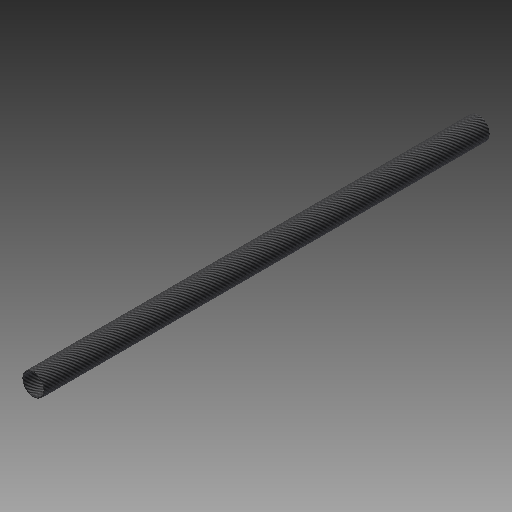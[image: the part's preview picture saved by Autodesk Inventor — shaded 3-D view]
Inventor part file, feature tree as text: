
AUTODESK INVENTOR PART (.ipt)
format: ipt  version: 2018 (Build 220112000, 112)  size: 120,832 bytes
history: native  units: in
note: dims shown in document units (in); Inventor stores cm internally (conversion verified against a paired STEP export)
features: extrude x1, sketch x1
ambient origin geometry x8: Origin, YZ Plane, XZ Plane, XY Plane, X Axis, Y Axis, Z Axis, Center Point
bodies: Solid1 (feature_tree)
feature tree (2):
  extrude  "Extrusion1"  Depth=0.4528in
  sketch  "Sketch1"  dims[d0=0.4921in d1=0.4528in d2=19.685in d3=0.0in]
